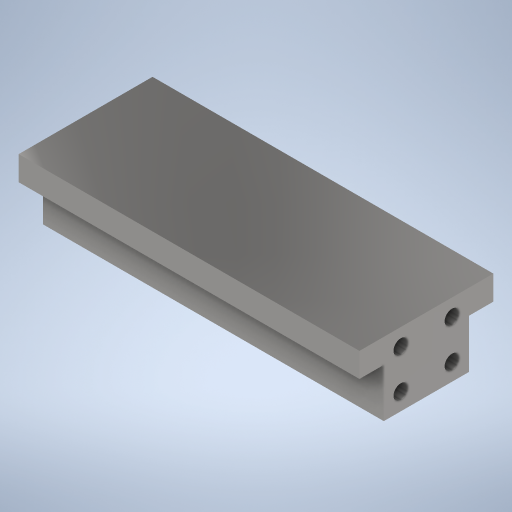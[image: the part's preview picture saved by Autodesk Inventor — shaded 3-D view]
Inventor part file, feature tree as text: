
AUTODESK INVENTOR PART (.ipt)
format: ipt  version: 2023.2 (Build 272271000, 271)  size: 311,296 bytes
history: native  units: mm
features: sketch x4, hole x3, extrude x1
ambient origin geometry x8: Origin, YZ Plane, XZ Plane, XY Plane, X Axis, Y Axis, Z Axis, Center Point
bodies: Solid1 (feature_tree)
feature tree (8):
  extrude  "Extrusion1"  Depth=10.0mm
  hole  "Hole2"  [1 undecoded]
  hole  "Hole3"  [1 undecoded]
  hole  "Hole4"  [1 undecoded]
  sketch  "Sketch1"  dims[d0=55.0mm d1=10.0mm]
  sketch  "Sketch3"  dims[d2=10.0mm d3=20.0mm]
  sketch  "Sketch4"  dims[d4=35.0mm d5=20.0mm]
  sketch  "Sketch5"  dims[d6=10.0mm d7=30.0mm d8=0.0mm d9=140.0mm d10=0.0mm d26=7.0mm d27=7.0mm d28=7.0mm d29=7.0mm d30=7.0mm d31=7.0mm d32=7.0mm d33=7.0mm d34=4.917mm d35=12.0mm d36=6.0mm d37=15.0mm d38=90.0deg d39=20.0mm d40=20.594885mm d41=8.0mm d42=23.0mm d43=23.0mm d44=7.0mm d45=7.0mm d46=4.917mm d47=12.0mm d48=6.0mm d49=15.0mm d50=90.0deg d51=20.0mm d52=20.594885mm d53=25.0mm d54=5.133974mm d55=12.0mm d56=10.0mm d57=2.0mm d58=90.0deg d59=16.2mm d60=20.594885mm d61=25.0mm d62=15.0mm d63=15.0mm d64=15.0mm d65=15.0mm d66=15.0mm d67=15.0mm d68=45.0mm d69=45.0mm d70=45.0mm d71=45.0mm d72=1.0mm d73=1.0mm d74=1.0mm d75=0.15mm d76=0.25mm d77=0.375mm d78=14.3117mm d79=0.75mm d80=20.594885mm d81=0.0625mm d82=0.75mm d83=0.375mm]
note: 3 required parameter values undecoded (feature->parameter linkage not recoverable at this tier; creation-order binding heuristic only, values carry confidence <= 0.55)
